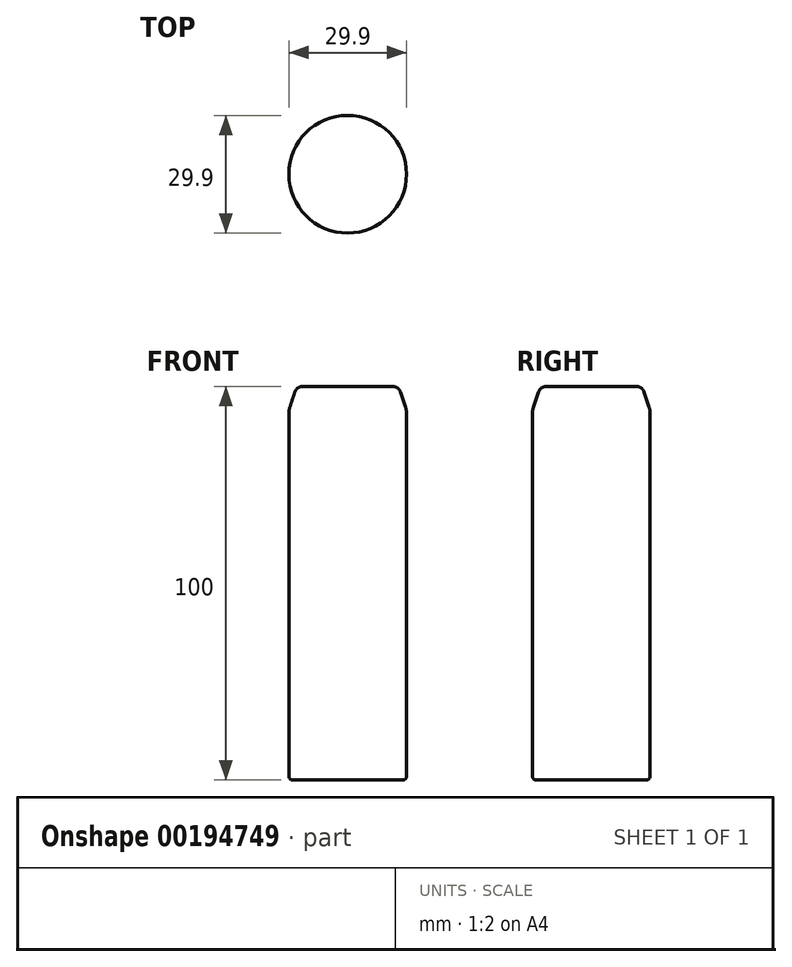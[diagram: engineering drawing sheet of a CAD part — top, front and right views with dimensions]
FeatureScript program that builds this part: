
annotation { "Feature Type Name" : "Feature", "Feature Type Description" : "" }
export const myFeature = defineFeature(function(context is Context, id is Id, definition is map)
    precondition{}
    {
        {
            var Q0;
            Q0=qCreatedBy(makeId("Top.planeOp"),FACE);
            var sketch = newSketch(context, id + "F0", { "sketchPlane" : qUnion([Q0])});
            skCircle(sketch, "E0", {"center": v(0, 1.48) * mm, "radius": 14.95 * mm});
            skSolve(sketch);
        }
        {
            var Q0;
            Q0 = qSketchRegion(id + "F0", true);
            extrude(context, id + "F1", {"entities" : qUnion([Q0]), "depth" : 100 * mm});
        }
        {
            var Q0;
            Q0=makeQuery(id+"F1.opExtrude","CAP_EDGE",EDGE,{"disambiguationData":[OSD([sQuery(id+"F0.wireOp",EDGE,"E0")])],"isStart":false});
            chamfer(context, id + "F2", {"entities" : qUnion([Q0]), "chamferType" : ChamferType.TWO_OFFSETS, "width1" : 2 * mm, "oppositeDirection" : false, "width2" : 6 * mm, "tangentPropagation" : true});
        }
        {
            var Q0;
            Q0=makeQuery(id+"F1.opExtrude","CAP_EDGE",EDGE,{"disambiguationData":[OSD([sQuery(id+"F0.wireOp",EDGE,"E0")])],"isStart":true});
            fillet(context, id + "F3", {"entities" : qUnion([Q0]), "radius" : 1 * mm, "tangentPropagation" : true, "allowEdgeOverflow" : false});
        }
        {
            var Q0;
            {var subQ0=sQuery(id+"F0.wireOp",EDGE,"E0");Q0=makeQuery(id+"F2.opChamfer","BLEND_EDGE",EDGE,{"blendedFrom":[makeQuery(id+"F1.opExtrude","CAP_EDGE",EDGE,{"disambiguationData":[OSD([subQ0])],"isStart":false}),makeQuery(id+"F1.opExtrude","CAP_FACE",FACE,{"disambiguationData":[OSD([subQ0])],"isStart":false})],"blendedInto":[makeQuery(id+"F1.opExtrude","CAP_FACE",FACE,{"disambiguationData":[OSD([subQ0])],"isStart":false})]});}
            fillet(context, id + "F4", {"entities" : qUnion([Q0]), "radius" : 2 * mm, "tangentPropagation" : true, "allowEdgeOverflow" : false});
        }
        {
            var Q0;
            {var subQ0=sQuery(id+"F0.wireOp",EDGE,"E0");Q0=makeQuery(id+"F2.opChamfer","BLEND_EDGE",EDGE,{"blendedFrom":[makeQuery(id+"F1.opExtrude","CAP_EDGE",EDGE,{"disambiguationData":[OSD([subQ0])],"isStart":false}),makeQuery(id+"F1.opExtrude","SWEPT_FACE",FACE,{"disambiguationData":[OSD([subQ0])]})],"blendedInto":[makeQuery(id+"F1.opExtrude","SWEPT_FACE",FACE,{"disambiguationData":[OSD([subQ0])]})]});}
            fillet(context, id + "F5", {"entities" : qUnion([Q0]), "radius" : 5 * mm, "tangentPropagation" : true, "allowEdgeOverflow" : false});
        }
    });
